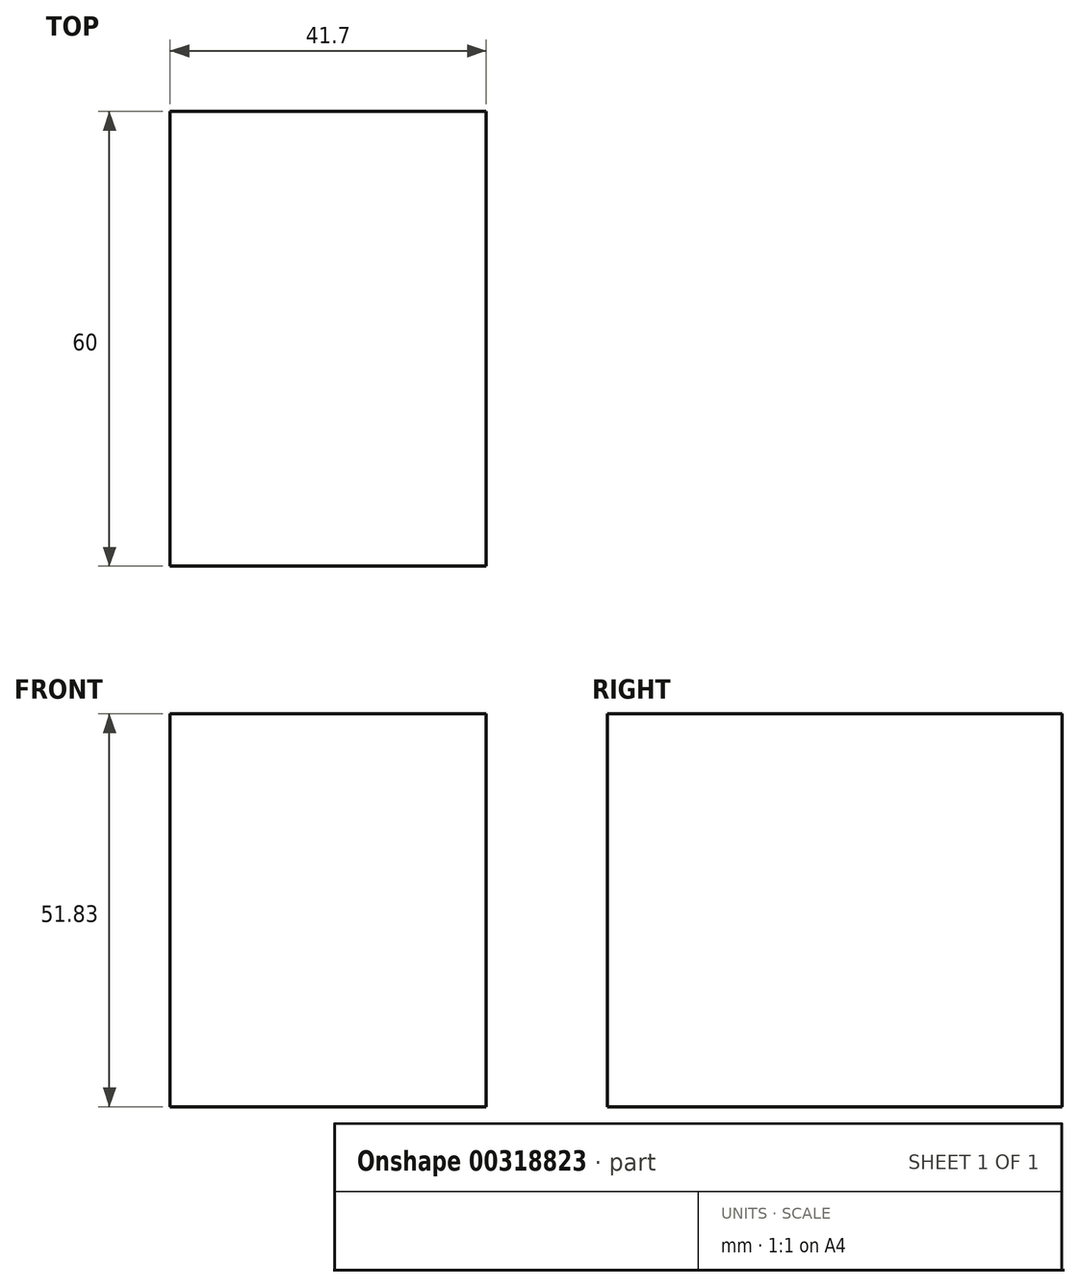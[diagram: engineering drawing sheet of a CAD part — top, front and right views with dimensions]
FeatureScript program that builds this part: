
annotation { "Feature Type Name" : "Feature", "Feature Type Description" : "" }
export const myFeature = defineFeature(function(context is Context, id is Id, definition is map)
    precondition{}
    {
        {
            var Q0;
            Q0=qCreatedBy(makeId("Front.planeOp"),FACE);
            var sketch = newSketch(context, id + "F0", { "sketchPlane" : qUnion([Q0])});
            skLineSegment(sketch, "E0.bottom", {"start": v(-32.06, 0) * mm, "end": v(9.64, 0) * mm});
            skLineSegment(sketch, "E0.top", {"start": v(-32.06, 51.83) * mm, "end": v(9.64, 51.83) * mm});
            skLineSegment(sketch, "E0.left", {"start": v(-32.06, 0) * mm, "end": v(-32.06, 51.83) * mm});
            skLineSegment(sketch, "E0.right", {"start": v(9.64, 0) * mm, "end": v(9.64, 51.83) * mm});
            skSolve(sketch);
        }
        {
            var Q0;
            Q0=makeQuery(id+"F0.imprint","IMPRINT",FACE,{"disambiguationData":[TD([[makeQuery(id+"F0.imprint","IMPRINT",EDGE,{"derivedFrom":sQuery(id+"F0.wireOp",EDGE,"E0.bottom")}),1.0]])]});
            extrude(context, id + "F1", {"entities" : qUnion([Q0]), "depth" : 60 * mm});
        }
    });
